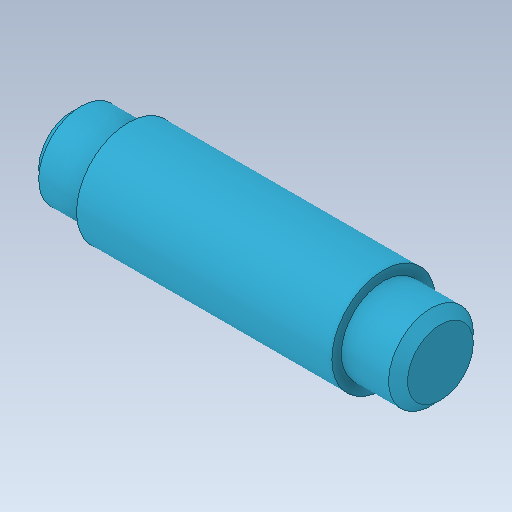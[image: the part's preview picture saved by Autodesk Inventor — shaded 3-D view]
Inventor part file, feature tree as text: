
AUTODESK INVENTOR PART (.ipt)
format: ipt  version: 2020 (Build 240168000, 168)  size: 122,368 bytes
history: native  units: mm
features: chamfer x2, revolve x1, sketch x1
ambient origin geometry x8: Origin, YZ Plane, XZ Plane, XY Plane, X Axis, Y Axis, Z Axis, Center Point
bodies: Solid1 (feature_tree)
feature tree (4):
  revolve  "Revolution1"  [1 undecoded]
  chamfer  "Chamfer1"  Distance=12.0mm
  chamfer  "Chamfer2"  Distance=2.0mm
  sketch  "Sketch1"  dims[d0=78.0mm d1=8.95mm d2=12.0mm d3=2.0mm d4=54.0mm d5=2.0mm d6=90.0deg d7=2.0mm d8=2.0mm d9=45.0deg d10=2.0mm d11=2.0mm d12=45.0deg]
note: 1 required parameter value undecoded (feature->parameter linkage not recoverable at this tier; creation-order binding heuristic only, values carry confidence <= 0.55)
